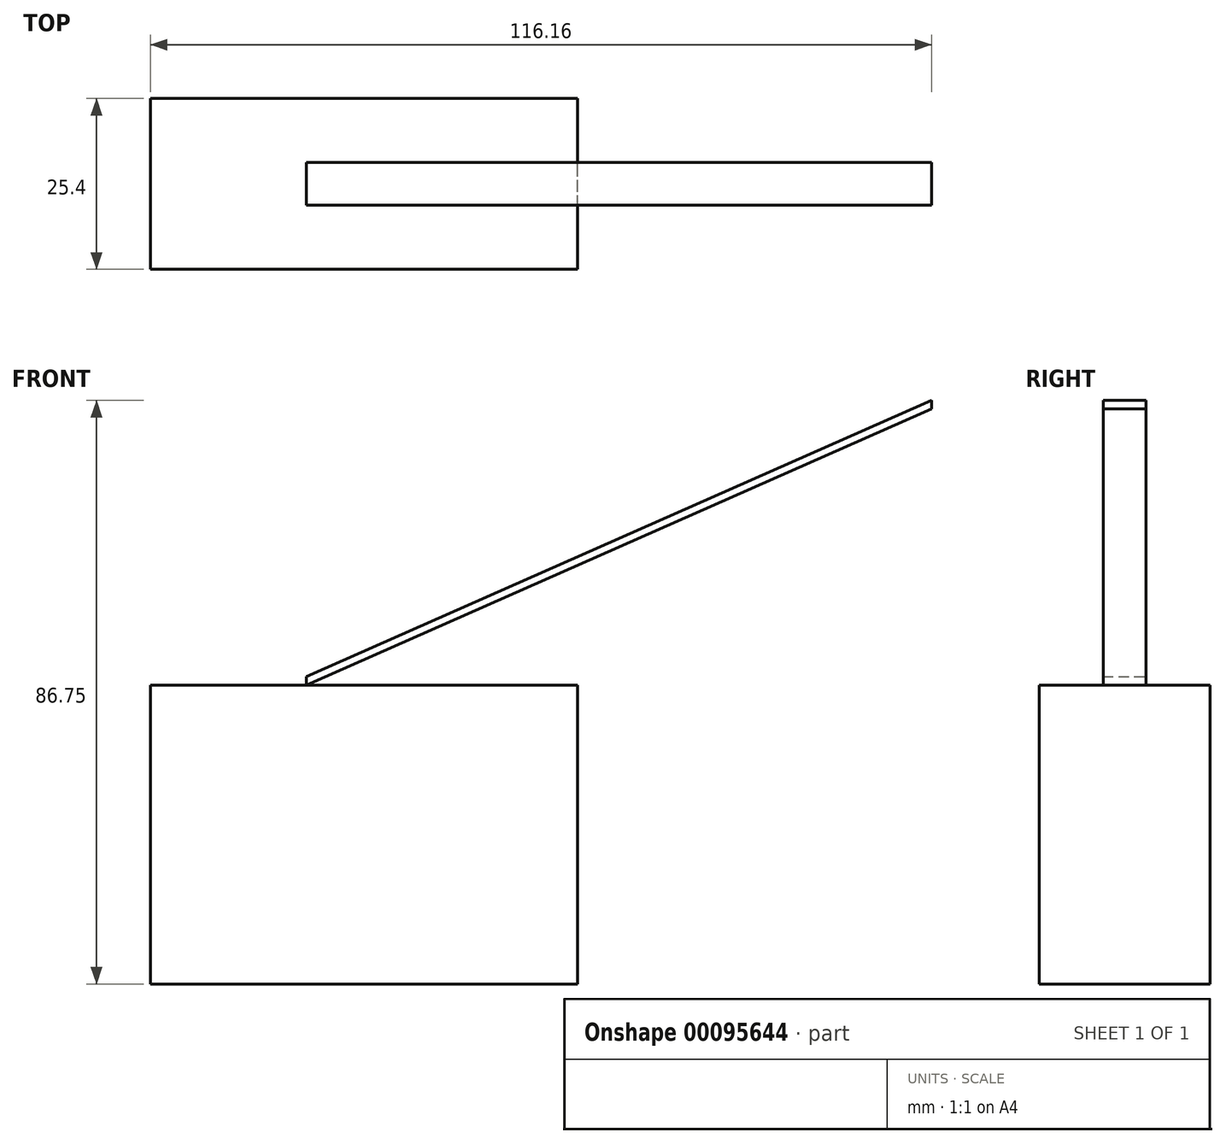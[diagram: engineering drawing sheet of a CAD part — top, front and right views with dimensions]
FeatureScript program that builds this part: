
annotation { "Feature Type Name" : "Feature", "Feature Type Description" : "" }
export const myFeature = defineFeature(function(context is Context, id is Id, definition is map)
    precondition{}
    {
        {
            var Q0;
            Q0=qCreatedBy(makeId("Front.planeOp"),FACE);
            var sketch = newSketch(context, id + "F0", { "sketchPlane" : qUnion([Q0])});
            skLineSegment(sketch, "E0.bottom", {"start": v(-26.26, 6.68) * mm, "end": v(37.24, 6.68) * mm});
            skLineSegment(sketch, "E0.top", {"start": v(-26.26, -37.77) * mm, "end": v(37.24, -37.77) * mm});
            skLineSegment(sketch, "E0.left", {"start": v(-26.26, 6.68) * mm, "end": v(-26.26, -37.77) * mm});
            skLineSegment(sketch, "E0.right", {"start": v(37.24, 6.68) * mm, "end": v(37.24, -37.77) * mm});
            skLineSegment(sketch, "E1", {"start": v(-3.05, 6.68) * mm, "end": v(-3.05, 7.95) * mm});
            skLineSegment(sketch, "E2", {"start": v(-3.05, 7.95) * mm, "end": v(89.9, 48.98) * mm});
            skLineSegment(sketch, "E3", {"start": v(89.9, 47.7) * mm, "end": v(89.9, 48.98) * mm});
            skLineSegment(sketch, "E4", {"start": v(89.9, 47.7) * mm, "end": v(-3.05, 6.68) * mm});
            skSolve(sketch);
        }
        {
            var Q0;
            Q0=makeQuery(id+"F0.imprint","IMPRINT",FACE,{"disambiguationData":[TD([[makeQuery(id+"F0.imprint","IMPRINT",EDGE,{"derivedFrom":sQuery(id+"F0.wireOp",EDGE,"E0.top")}),1.0]])]});
            extrude(context, id + "F1", {"entities" : qUnion([Q0]), "endBound" : BoundingType.SYMMETRIC, "depth" : 25.4 * mm});
        }
        {
            var Q0;
            Q0=makeQuery(id+"F0.imprint","IMPRINT",FACE,{"disambiguationData":[TD([[makeQuery(id+"F0.imprint","IMPRINT",EDGE,{"derivedFrom":sQuery(id+"F0.wireOp",EDGE,"E1")}),-1.0]])]});
            extrude(context, id + "F2", {"entities" : qUnion([Q0]), "endBound" : BoundingType.SYMMETRIC, "depth" : 6.35 * mm});
        }
    });
